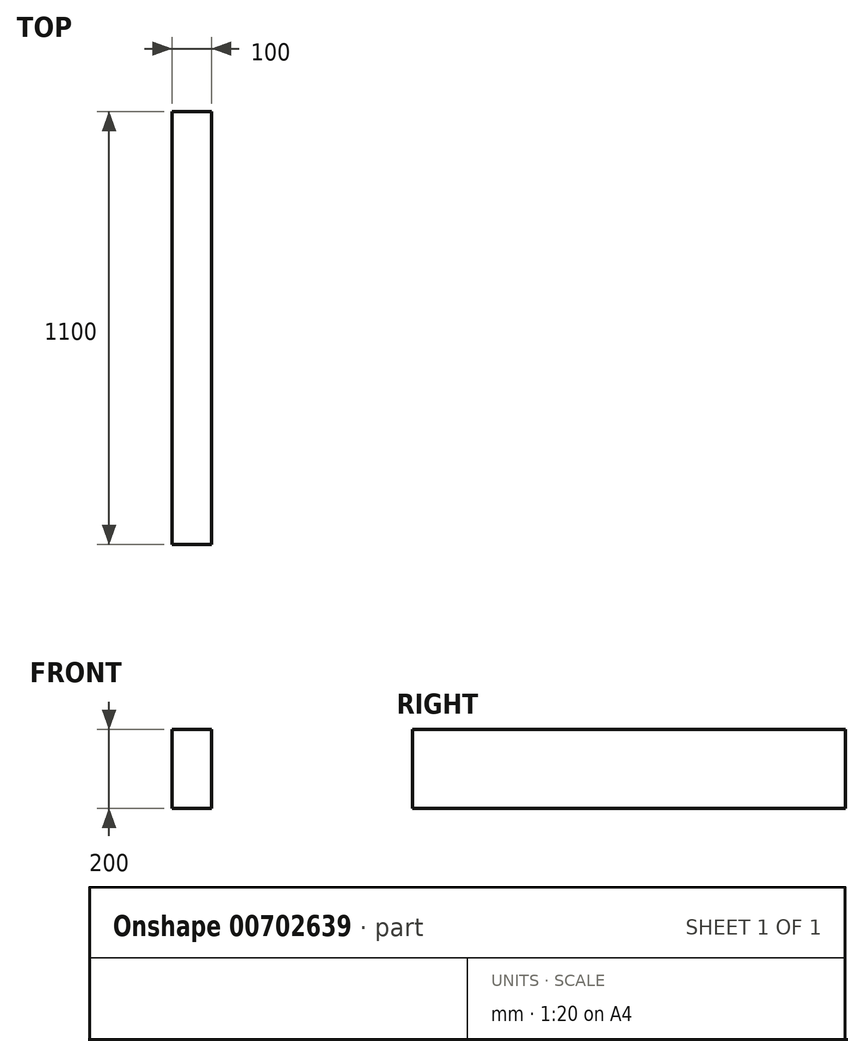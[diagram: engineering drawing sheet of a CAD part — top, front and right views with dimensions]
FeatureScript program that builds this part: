
annotation { "Feature Type Name" : "Feature", "Feature Type Description" : "" }
export const myFeature = defineFeature(function(context is Context, id is Id, definition is map)
    precondition{}
    {
        {
            var Q0;
            Q0=qCreatedBy(makeId("Front.planeOp"),FACE);
            var sketch = newSketch(context, id + "F0", { "sketchPlane" : qUnion([Q0])});
            skLineSegment(sketch, "E0.bottom", {"start": v(0, 0) * mm, "end": v(-100, 0) * mm});
            skLineSegment(sketch, "E0.top", {"start": v(0, 200) * mm, "end": v(-100, 200) * mm});
            skLineSegment(sketch, "E0.left", {"start": v(0, 0) * mm, "end": v(0, 200) * mm});
            skLineSegment(sketch, "E0.right", {"start": v(-100, 0) * mm, "end": v(-100, 200) * mm});
            skSolve(sketch);
        }
        {
            var Q0;
            Q0=qSketchRegion(id+"F0",true);
            extrude(context, id + "F1", {"entities" : qUnion([Q0]), "depth" : 1100 * mm, "offsetDistance" : 25 * mm});
        }
    });
